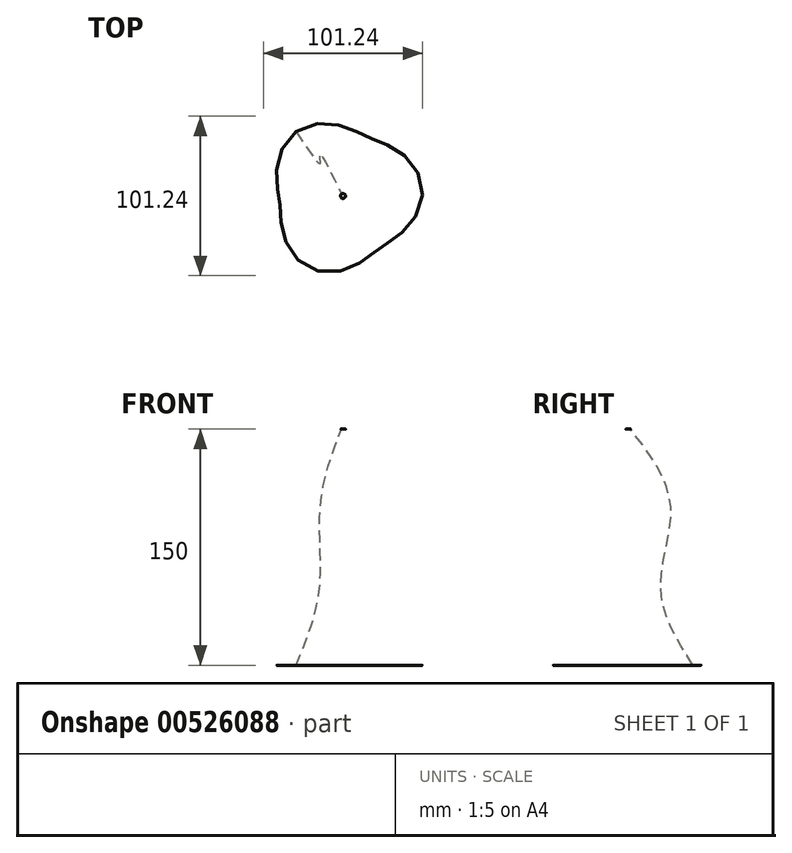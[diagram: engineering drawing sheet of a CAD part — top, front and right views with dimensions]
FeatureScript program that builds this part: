
annotation { "Feature Type Name" : "Feature", "Feature Type Description" : "" }
export const myFeature = defineFeature(function(context is Context, id is Id, definition is map)
    precondition{}
    {
        {
            var Q0;
            Q0=qCreatedBy(makeId("Top.planeOp"),FACE);
            var sketch = newSketch(context, id + "F0", { "sketchPlane" : qUnion([Q0])});
            skCircle(sketch, "E0.cCircle", {"center": v(0, 0) * mm, "radius": 50 * mm, "construction": true});
            skLineSegment(sketch, "E0.0", {"start": v(-40.96, 29.76) * mm, "end": v(-29.76, 40.96) * mm, "construction": true});
            skLineSegment(sketch, "E0.1", {"start": v(-29.76, 40.96) * mm, "end": v(-15.64, 48.15) * mm, "construction": true});
            skLineSegment(sketch, "E0.2", {"start": v(-15.64, 48.15) * mm, "end": v(0, 50.62) * mm, "construction": true});
            skLineSegment(sketch, "E0.3", {"start": v(0, 50.62) * mm, "end": v(15.64, 48.15) * mm, "construction": true});
            skLineSegment(sketch, "E0.4", {"start": v(15.64, 48.15) * mm, "end": v(29.76, 40.96) * mm, "construction": true});
            skLineSegment(sketch, "E0.5", {"start": v(29.76, 40.96) * mm, "end": v(40.96, 29.76) * mm, "construction": true});
            skLineSegment(sketch, "E0.6", {"start": v(40.96, 29.76) * mm, "end": v(48.15, 15.64) * mm, "construction": true});
            skLineSegment(sketch, "E0.7", {"start": v(48.15, 15.64) * mm, "end": v(50.62, 0) * mm, "construction": true});
            skLineSegment(sketch, "E0.8", {"start": v(50.62, 0) * mm, "end": v(48.15, -15.64) * mm, "construction": true});
            skLineSegment(sketch, "E0.9", {"start": v(48.15, -15.64) * mm, "end": v(40.96, -29.76) * mm, "construction": true});
            skLineSegment(sketch, "E0.10", {"start": v(40.96, -29.76) * mm, "end": v(29.76, -40.96) * mm, "construction": true});
            skLineSegment(sketch, "E0.11", {"start": v(29.76, -40.96) * mm, "end": v(15.64, -48.15) * mm, "construction": true});
            skLineSegment(sketch, "E0.12", {"start": v(15.64, -48.15) * mm, "end": v(0, -50.62) * mm, "construction": true});
            skLineSegment(sketch, "E0.13", {"start": v(0, -50.62) * mm, "end": v(-15.64, -48.15) * mm, "construction": true});
            skLineSegment(sketch, "E0.14", {"start": v(-15.64, -48.15) * mm, "end": v(-29.76, -40.96) * mm, "construction": true});
            skLineSegment(sketch, "E0.15", {"start": v(-29.76, -40.96) * mm, "end": v(-40.96, -29.76) * mm, "construction": true});
            skLineSegment(sketch, "E0.16", {"start": v(-40.96, -29.76) * mm, "end": v(-48.15, -15.64) * mm, "construction": true});
            skLineSegment(sketch, "E0.17", {"start": v(-48.15, -15.64) * mm, "end": v(-50.62, 0) * mm, "construction": true});
            skLineSegment(sketch, "E0.18", {"start": v(-50.62, 0) * mm, "end": v(-48.15, 15.64) * mm, "construction": true});
            skLineSegment(sketch, "E0.19", {"start": v(-48.15, 15.64) * mm, "end": v(-40.96, 29.76) * mm, "construction": true});
            skPoint(sketch, "E0.0.midPoint", {"position": v(-35.36, 35.36) * mm});
            skCircle(sketch, "E1.cCircle", {"center": v(0, 0) * mm, "radius": 40 * mm, "construction": true});
            skLineSegment(sketch, "E1.0", {"start": v(-18.39, 36.08) * mm, "end": v(-6.34, 40) * mm, "construction": true});
            skLineSegment(sketch, "E1.1", {"start": v(-6.34, 40) * mm, "end": v(6.34, 40) * mm, "construction": true});
            skLineSegment(sketch, "E1.2", {"start": v(6.34, 40) * mm, "end": v(18.39, 36.08) * mm, "construction": true});
            skLineSegment(sketch, "E1.3", {"start": v(18.39, 36.08) * mm, "end": v(28.64, 28.64) * mm, "construction": true});
            skLineSegment(sketch, "E1.4", {"start": v(28.64, 28.64) * mm, "end": v(36.08, 18.39) * mm, "construction": true});
            skLineSegment(sketch, "E1.5", {"start": v(36.08, 18.39) * mm, "end": v(40, 6.34) * mm, "construction": true});
            skLineSegment(sketch, "E1.6", {"start": v(40, 6.34) * mm, "end": v(40, -6.34) * mm, "construction": true});
            skLineSegment(sketch, "E1.7", {"start": v(40, -6.34) * mm, "end": v(36.08, -18.39) * mm, "construction": true});
            skLineSegment(sketch, "E1.8", {"start": v(36.08, -18.39) * mm, "end": v(28.64, -28.64) * mm, "construction": true});
            skLineSegment(sketch, "E1.9", {"start": v(28.64, -28.64) * mm, "end": v(18.39, -36.08) * mm, "construction": true});
            skLineSegment(sketch, "E1.10", {"start": v(18.39, -36.08) * mm, "end": v(6.34, -40) * mm, "construction": true});
            skLineSegment(sketch, "E1.11", {"start": v(6.34, -40) * mm, "end": v(-6.34, -40) * mm, "construction": true});
            skLineSegment(sketch, "E1.12", {"start": v(-6.34, -40) * mm, "end": v(-18.39, -36.08) * mm, "construction": true});
            skLineSegment(sketch, "E1.13", {"start": v(-18.39, -36.08) * mm, "end": v(-28.64, -28.64) * mm, "construction": true});
            skLineSegment(sketch, "E1.14", {"start": v(-28.64, -28.64) * mm, "end": v(-36.08, -18.39) * mm, "construction": true});
            skLineSegment(sketch, "E1.15", {"start": v(-36.08, -18.39) * mm, "end": v(-40, -6.34) * mm, "construction": true});
            skLineSegment(sketch, "E1.16", {"start": v(-40, -6.34) * mm, "end": v(-40, 6.34) * mm, "construction": true});
            skLineSegment(sketch, "E1.17", {"start": v(-40, 6.34) * mm, "end": v(-36.08, 18.39) * mm, "construction": true});
            skLineSegment(sketch, "E1.18", {"start": v(-36.08, 18.39) * mm, "end": v(-28.64, 28.64) * mm, "construction": true});
            skLineSegment(sketch, "E1.19", {"start": v(-28.64, 28.64) * mm, "end": v(-18.39, 36.08) * mm, "construction": true});
            skPoint(sketch, "E1.0.midPoint", {"position": v(-12.36, 38.04) * mm});
            skLineSegment(sketch, "E2", {"start": v(0, 0) * mm, "end": v(0, 40) * mm, "construction": true});
            skFitSpline(sketch, "E3", {"points": [v(-29.76, 40.96) * mm, v(-18.39, 36.08) * mm, v(-15.64, 48.15) * mm, v(-6.34, 40) * mm, v(0, 50.62) * mm, v(6.34, 40) * mm, v(15.64, 48.15) * mm, v(18.39, 36.08) * mm, v(29.76, 40.96) * mm, v(28.64, 28.64) * mm, v(40.96, 29.76) * mm, v(36.08, 18.39) * mm, v(48.15, 15.64) * mm, v(40, 6.34) * mm, v(50.62, 0) * mm, v(40, -6.34) * mm, v(48.15, -15.64) * mm, v(36.08, -18.39) * mm, v(40.96, -29.76) * mm, v(28.64, -28.64) * mm, v(29.76, -40.96) * mm, v(18.39, -36.08) * mm, v(15.64, -48.15) * mm, v(6.34, -40) * mm, v(0, -50.62) * mm, v(-6.34, -40) * mm, v(-15.64, -48.15) * mm, v(-18.39, -36.08) * mm, v(-29.76, -40.96) * mm, v(-28.64, -28.64) * mm, v(-40.96, -29.76) * mm, v(-36.08, -18.39) * mm, v(-48.15, -15.64) * mm, v(-40, -6.34) * mm, v(-50.62, 0) * mm, v(-40, 6.34) * mm, v(-48.15, 15.64) * mm, v(-36.08, 18.39) * mm, v(-40.96, 29.76) * mm, v(-28.64, 28.64) * mm, v(-29.76, 40.96) * mm]});
            skSolve(sketch);
        }
        {
            var Q0;
            Q0=qCreatedBy(makeId("Top.planeOp"),FACE);
            cPlane(context, id + "F1", {"entities" : qUnion([Q0]), "cplaneType" : CPlaneType.OFFSET, "offset" : 50 * mm, "width" : 150 * mm, "height" : 150 * mm});
        }
        {
            var Q0;
            Q0=qCreatedBy(id+"F1.planeOp",FACE);
            var sketch = newSketch(context, id + "F2", { "sketchPlane" : qUnion([Q0])});
            skCircle(sketch, "E4.cCircle", {"center": v(0, 0) * mm, "radius": 25 * mm, "construction": true});
            skLineSegment(sketch, "E4.0", {"start": v(-20.48, 14.88) * mm, "end": v(-14.88, 20.48) * mm, "construction": true});
            skLineSegment(sketch, "E4.1", {"start": v(-14.88, 20.48) * mm, "end": v(-7.82, 24.07) * mm, "construction": true});
            skLineSegment(sketch, "E4.2", {"start": v(-7.82, 24.07) * mm, "end": v(0, 25.31) * mm, "construction": true});
            skLineSegment(sketch, "E4.3", {"start": v(0, 25.31) * mm, "end": v(7.82, 24.07) * mm, "construction": true});
            skLineSegment(sketch, "E4.4", {"start": v(7.82, 24.07) * mm, "end": v(14.88, 20.48) * mm, "construction": true});
            skLineSegment(sketch, "E4.5", {"start": v(14.88, 20.48) * mm, "end": v(20.48, 14.88) * mm, "construction": true});
            skLineSegment(sketch, "E4.6", {"start": v(20.48, 14.88) * mm, "end": v(24.07, 7.82) * mm, "construction": true});
            skLineSegment(sketch, "E4.7", {"start": v(24.07, 7.82) * mm, "end": v(25.31, 0) * mm, "construction": true});
            skLineSegment(sketch, "E4.8", {"start": v(25.31, 0) * mm, "end": v(24.07, -7.82) * mm, "construction": true});
            skLineSegment(sketch, "E4.9", {"start": v(24.07, -7.82) * mm, "end": v(20.48, -14.88) * mm, "construction": true});
            skLineSegment(sketch, "E4.10", {"start": v(20.48, -14.88) * mm, "end": v(14.88, -20.48) * mm, "construction": true});
            skLineSegment(sketch, "E4.11", {"start": v(14.88, -20.48) * mm, "end": v(7.82, -24.07) * mm, "construction": true});
            skLineSegment(sketch, "E4.12", {"start": v(7.82, -24.07) * mm, "end": v(0, -25.31) * mm, "construction": true});
            skLineSegment(sketch, "E4.13", {"start": v(0, -25.31) * mm, "end": v(-7.82, -24.07) * mm, "construction": true});
            skLineSegment(sketch, "E4.14", {"start": v(-7.82, -24.07) * mm, "end": v(-14.88, -20.48) * mm, "construction": true});
            skLineSegment(sketch, "E4.15", {"start": v(-14.88, -20.48) * mm, "end": v(-20.48, -14.88) * mm, "construction": true});
            skLineSegment(sketch, "E4.16", {"start": v(-20.48, -14.88) * mm, "end": v(-24.07, -7.82) * mm, "construction": true});
            skLineSegment(sketch, "E4.17", {"start": v(-24.07, -7.82) * mm, "end": v(-25.31, 0) * mm, "construction": true});
            skLineSegment(sketch, "E4.18", {"start": v(-25.31, 0) * mm, "end": v(-24.07, 7.82) * mm, "construction": true});
            skLineSegment(sketch, "E4.19", {"start": v(-24.07, 7.82) * mm, "end": v(-20.48, 14.88) * mm, "construction": true});
            skPoint(sketch, "E4.0.midPoint", {"position": v(-17.68, 17.68) * mm});
            skCircle(sketch, "E5.cCircle", {"center": v(0, 0) * mm, "radius": 20 * mm, "construction": true});
            skLineSegment(sketch, "E5.0", {"start": v(-9.2, 18.04) * mm, "end": v(-3.17, 20) * mm, "construction": true});
            skLineSegment(sketch, "E5.1", {"start": v(-3.17, 20) * mm, "end": v(3.17, 20) * mm, "construction": true});
            skLineSegment(sketch, "E5.2", {"start": v(3.17, 20) * mm, "end": v(9.2, 18.04) * mm, "construction": true});
            skLineSegment(sketch, "E5.3", {"start": v(9.2, 18.04) * mm, "end": v(14.32, 14.32) * mm, "construction": true});
            skLineSegment(sketch, "E5.4", {"start": v(14.32, 14.32) * mm, "end": v(18.04, 9.2) * mm, "construction": true});
            skLineSegment(sketch, "E5.5", {"start": v(18.04, 9.2) * mm, "end": v(20, 3.17) * mm, "construction": true});
            skLineSegment(sketch, "E5.6", {"start": v(20, 3.17) * mm, "end": v(20, -3.17) * mm, "construction": true});
            skLineSegment(sketch, "E5.7", {"start": v(20, -3.17) * mm, "end": v(18.04, -9.2) * mm, "construction": true});
            skLineSegment(sketch, "E5.8", {"start": v(18.04, -9.2) * mm, "end": v(14.32, -14.32) * mm, "construction": true});
            skLineSegment(sketch, "E5.9", {"start": v(14.32, -14.32) * mm, "end": v(9.2, -18.04) * mm, "construction": true});
            skLineSegment(sketch, "E5.10", {"start": v(9.2, -18.04) * mm, "end": v(3.17, -20) * mm, "construction": true});
            skLineSegment(sketch, "E5.11", {"start": v(3.17, -20) * mm, "end": v(-3.17, -20) * mm, "construction": true});
            skLineSegment(sketch, "E5.12", {"start": v(-3.17, -20) * mm, "end": v(-9.2, -18.04) * mm, "construction": true});
            skLineSegment(sketch, "E5.13", {"start": v(-9.2, -18.04) * mm, "end": v(-14.32, -14.32) * mm, "construction": true});
            skLineSegment(sketch, "E5.14", {"start": v(-14.32, -14.32) * mm, "end": v(-18.04, -9.2) * mm, "construction": true});
            skLineSegment(sketch, "E5.15", {"start": v(-18.04, -9.2) * mm, "end": v(-20, -3.17) * mm, "construction": true});
            skLineSegment(sketch, "E5.16", {"start": v(-20, -3.17) * mm, "end": v(-20, 3.17) * mm, "construction": true});
            skLineSegment(sketch, "E5.17", {"start": v(-20, 3.17) * mm, "end": v(-18.04, 9.2) * mm, "construction": true});
            skLineSegment(sketch, "E5.18", {"start": v(-18.04, 9.2) * mm, "end": v(-14.32, 14.32) * mm, "construction": true});
            skLineSegment(sketch, "E5.19", {"start": v(-14.32, 14.32) * mm, "end": v(-9.2, 18.04) * mm, "construction": true});
            skPoint(sketch, "E5.0.midPoint", {"position": v(-6.18, 19.02) * mm});
            skLineSegment(sketch, "E6", {"start": v(0, 0) * mm, "end": v(0, 20) * mm, "construction": true});
            skFitSpline(sketch, "E7", {"points": [v(-14.88, 20.48) * mm, v(-9.2, 18.04) * mm, v(-7.82, 24.07) * mm, v(-3.17, 20) * mm, v(0, 25.31) * mm, v(3.17, 20) * mm, v(7.82, 24.07) * mm, v(9.2, 18.04) * mm, v(14.88, 20.48) * mm, v(14.32, 14.32) * mm, v(20.48, 14.88) * mm, v(18.04, 9.2) * mm, v(24.07, 7.82) * mm, v(20, 3.17) * mm, v(25.31, 0) * mm, v(20, -3.17) * mm, v(24.07, -7.82) * mm, v(18.04, -9.2) * mm, v(20.48, -14.88) * mm, v(14.32, -14.32) * mm, v(14.88, -20.48) * mm, v(9.2, -18.04) * mm, v(7.82, -24.07) * mm, v(3.17, -20) * mm, v(0, -25.31) * mm, v(-3.17, -20) * mm, v(-7.82, -24.07) * mm, v(-9.2, -18.04) * mm, v(-14.88, -20.48) * mm, v(-14.32, -14.32) * mm, v(-20.48, -14.88) * mm, v(-18.04, -9.2) * mm, v(-24.07, -7.82) * mm, v(-20, -3.17) * mm, v(-25.31, 0) * mm, v(-20, 3.17) * mm, v(-24.07, 7.82) * mm, v(-18.04, 9.2) * mm, v(-20.48, 14.88) * mm, v(-14.32, 14.32) * mm, v(-14.88, 20.48) * mm]});
            skSolve(sketch);
        }
        {
            var Q0;
            Q0=qCreatedBy(id+"F1.planeOp",FACE);
            cPlane(context, id + "F3", {"entities" : qUnion([Q0]), "cplaneType" : CPlaneType.OFFSET, "offset" : 50 * mm, "width" : 150 * mm, "height" : 150 * mm});
        }
        {
            var Q0;
            Q0=qCreatedBy(id+"F3.planeOp",FACE);
            var sketch = newSketch(context, id + "F4", { "sketchPlane" : qUnion([Q0])});
            skCircle(sketch, "E8.cCircle", {"center": v(0, 0) * mm, "radius": 40 * mm, "construction": true});
            skLineSegment(sketch, "E8.0", {"start": v(-32.76, 23.8) * mm, "end": v(-23.8, 32.76) * mm, "construction": true});
            skLineSegment(sketch, "E8.1", {"start": v(-23.8, 32.76) * mm, "end": v(-12.51, 38.52) * mm, "construction": true});
            skLineSegment(sketch, "E8.2", {"start": v(-12.51, 38.52) * mm, "end": v(0, 40.5) * mm, "construction": true});
            skLineSegment(sketch, "E8.3", {"start": v(0, 40.5) * mm, "end": v(12.51, 38.52) * mm, "construction": true});
            skLineSegment(sketch, "E8.4", {"start": v(12.51, 38.52) * mm, "end": v(23.8, 32.76) * mm, "construction": true});
            skLineSegment(sketch, "E8.5", {"start": v(23.8, 32.76) * mm, "end": v(32.76, 23.8) * mm, "construction": true});
            skLineSegment(sketch, "E8.6", {"start": v(32.76, 23.8) * mm, "end": v(38.52, 12.51) * mm, "construction": true});
            skLineSegment(sketch, "E8.7", {"start": v(38.52, 12.51) * mm, "end": v(40.5, 0) * mm, "construction": true});
            skLineSegment(sketch, "E8.8", {"start": v(40.5, 0) * mm, "end": v(38.52, -12.51) * mm, "construction": true});
            skLineSegment(sketch, "E8.9", {"start": v(38.52, -12.51) * mm, "end": v(32.76, -23.8) * mm, "construction": true});
            skLineSegment(sketch, "E8.10", {"start": v(32.76, -23.8) * mm, "end": v(23.8, -32.76) * mm, "construction": true});
            skLineSegment(sketch, "E8.11", {"start": v(23.8, -32.76) * mm, "end": v(12.51, -38.52) * mm, "construction": true});
            skLineSegment(sketch, "E8.12", {"start": v(12.51, -38.52) * mm, "end": v(0, -40.5) * mm, "construction": true});
            skLineSegment(sketch, "E8.13", {"start": v(0, -40.5) * mm, "end": v(-12.51, -38.52) * mm, "construction": true});
            skLineSegment(sketch, "E8.14", {"start": v(-12.51, -38.52) * mm, "end": v(-23.8, -32.76) * mm, "construction": true});
            skLineSegment(sketch, "E8.15", {"start": v(-23.8, -32.76) * mm, "end": v(-32.76, -23.8) * mm, "construction": true});
            skLineSegment(sketch, "E8.16", {"start": v(-32.76, -23.8) * mm, "end": v(-38.52, -12.51) * mm, "construction": true});
            skLineSegment(sketch, "E8.17", {"start": v(-38.52, -12.51) * mm, "end": v(-40.5, 0) * mm, "construction": true});
            skLineSegment(sketch, "E8.18", {"start": v(-40.5, 0) * mm, "end": v(-38.52, 12.51) * mm, "construction": true});
            skLineSegment(sketch, "E8.19", {"start": v(-38.52, 12.51) * mm, "end": v(-32.76, 23.8) * mm, "construction": true});
            skPoint(sketch, "E8.0.midPoint", {"position": v(-28.28, 28.28) * mm});
            skCircle(sketch, "E9.cCircle", {"center": v(0, 0) * mm, "radius": 30 * mm, "construction": true});
            skLineSegment(sketch, "E9.0", {"start": v(-13.79, 27.06) * mm, "end": v(-4.75, 30) * mm, "construction": true});
            skLineSegment(sketch, "E9.1", {"start": v(-4.75, 30) * mm, "end": v(4.75, 30) * mm, "construction": true});
            skLineSegment(sketch, "E9.2", {"start": v(4.75, 30) * mm, "end": v(13.79, 27.06) * mm, "construction": true});
            skLineSegment(sketch, "E9.3", {"start": v(13.79, 27.06) * mm, "end": v(21.48, 21.48) * mm, "construction": true});
            skLineSegment(sketch, "E9.4", {"start": v(21.48, 21.48) * mm, "end": v(27.06, 13.79) * mm, "construction": true});
            skLineSegment(sketch, "E9.5", {"start": v(27.06, 13.79) * mm, "end": v(30, 4.75) * mm, "construction": true});
            skLineSegment(sketch, "E9.6", {"start": v(30, 4.75) * mm, "end": v(30, -4.75) * mm, "construction": true});
            skLineSegment(sketch, "E9.7", {"start": v(30, -4.75) * mm, "end": v(27.06, -13.79) * mm, "construction": true});
            skLineSegment(sketch, "E9.8", {"start": v(27.06, -13.79) * mm, "end": v(21.48, -21.48) * mm, "construction": true});
            skLineSegment(sketch, "E9.9", {"start": v(21.48, -21.48) * mm, "end": v(13.79, -27.06) * mm, "construction": true});
            skLineSegment(sketch, "E9.10", {"start": v(13.79, -27.06) * mm, "end": v(4.75, -30) * mm, "construction": true});
            skLineSegment(sketch, "E9.11", {"start": v(4.75, -30) * mm, "end": v(-4.75, -30) * mm, "construction": true});
            skLineSegment(sketch, "E9.12", {"start": v(-4.75, -30) * mm, "end": v(-13.79, -27.06) * mm, "construction": true});
            skLineSegment(sketch, "E9.13", {"start": v(-13.79, -27.06) * mm, "end": v(-21.48, -21.48) * mm, "construction": true});
            skLineSegment(sketch, "E9.14", {"start": v(-21.48, -21.48) * mm, "end": v(-27.06, -13.79) * mm, "construction": true});
            skLineSegment(sketch, "E9.15", {"start": v(-27.06, -13.79) * mm, "end": v(-30, -4.75) * mm, "construction": true});
            skLineSegment(sketch, "E9.16", {"start": v(-30, -4.75) * mm, "end": v(-30, 4.75) * mm, "construction": true});
            skLineSegment(sketch, "E9.17", {"start": v(-30, 4.75) * mm, "end": v(-27.06, 13.79) * mm, "construction": true});
            skLineSegment(sketch, "E9.18", {"start": v(-27.06, 13.79) * mm, "end": v(-21.48, 21.48) * mm, "construction": true});
            skLineSegment(sketch, "E9.19", {"start": v(-21.48, 21.48) * mm, "end": v(-13.79, 27.06) * mm, "construction": true});
            skPoint(sketch, "E9.0.midPoint", {"position": v(-9.27, 28.53) * mm});
            skLineSegment(sketch, "E10", {"start": v(0, 0) * mm, "end": v(0, 30) * mm, "construction": true});
            skFitSpline(sketch, "E11", {"points": [v(-23.8, 32.76) * mm, v(-13.79, 27.06) * mm, v(-12.51, 38.52) * mm, v(-4.75, 30) * mm, v(0, 40.5) * mm, v(4.75, 30) * mm, v(12.51, 38.52) * mm, v(13.79, 27.06) * mm, v(23.8, 32.76) * mm, v(21.48, 21.48) * mm, v(32.76, 23.8) * mm, v(27.06, 13.79) * mm, v(38.52, 12.51) * mm, v(30, 4.75) * mm, v(40.5, 0) * mm, v(30, -4.75) * mm, v(38.52, -12.51) * mm, v(27.06, -13.79) * mm, v(32.76, -23.8) * mm, v(21.48, -21.48) * mm, v(23.8, -32.76) * mm, v(13.79, -27.06) * mm, v(12.51, -38.52) * mm, v(4.75, -30) * mm, v(0, -40.5) * mm, v(-4.75, -30) * mm, v(-12.51, -38.52) * mm, v(-13.79, -27.06) * mm, v(-23.8, -32.76) * mm, v(-21.48, -21.48) * mm, v(-32.76, -23.8) * mm, v(-27.06, -13.79) * mm, v(-38.52, -12.51) * mm, v(-30, -4.75) * mm, v(-40.5, 0) * mm, v(-30, 4.75) * mm, v(-38.52, 12.51) * mm, v(-27.06, 13.79) * mm, v(-32.76, 23.8) * mm, v(-21.48, 21.48) * mm, v(-23.8, 32.76) * mm]});
            skSolve(sketch);
        }
        {
            var Q0;
            Q0=qCreatedBy(id+"F3.planeOp",FACE);
            cPlane(context, id + "F5", {"entities" : qUnion([Q0]), "cplaneType" : CPlaneType.OFFSET, "offset" : 50 * mm, "width" : 150 * mm, "height" : 150 * mm});
        }
        {
            var Q0;
            Q0=qCreatedBy(id+"F5.planeOp",FACE);
            var sketch = newSketch(context, id + "F6", { "sketchPlane" : qUnion([Q0])});
            skCircle(sketch, "E12.cCircle", {"center": v(0, 0) * mm, "radius": 1.65 * mm, "construction": true});
            skLineSegment(sketch, "E12.0", {"start": v(-1.35, 0.98) * mm, "end": v(-0.98, 1.35) * mm, "construction": true});
            skLineSegment(sketch, "E12.1", {"start": v(-0.98, 1.35) * mm, "end": v(-0.52, 1.59) * mm, "construction": true});
            skLineSegment(sketch, "E12.2", {"start": v(-0.52, 1.59) * mm, "end": v(0, 1.67) * mm, "construction": true});
            skLineSegment(sketch, "E12.3", {"start": v(0, 1.67) * mm, "end": v(0.52, 1.59) * mm, "construction": true});
            skLineSegment(sketch, "E12.4", {"start": v(0.52, 1.59) * mm, "end": v(0.98, 1.35) * mm, "construction": true});
            skLineSegment(sketch, "E12.5", {"start": v(0.98, 1.35) * mm, "end": v(1.35, 0.98) * mm, "construction": true});
            skLineSegment(sketch, "E12.6", {"start": v(1.35, 0.98) * mm, "end": v(1.59, 0.52) * mm, "construction": true});
            skLineSegment(sketch, "E12.7", {"start": v(1.59, 0.52) * mm, "end": v(1.67, 0) * mm, "construction": true});
            skLineSegment(sketch, "E12.8", {"start": v(1.67, 0) * mm, "end": v(1.59, -0.52) * mm, "construction": true});
            skLineSegment(sketch, "E12.9", {"start": v(1.59, -0.52) * mm, "end": v(1.35, -0.98) * mm, "construction": true});
            skLineSegment(sketch, "E12.10", {"start": v(1.35, -0.98) * mm, "end": v(0.98, -1.35) * mm, "construction": true});
            skLineSegment(sketch, "E12.11", {"start": v(0.98, -1.35) * mm, "end": v(0.52, -1.59) * mm, "construction": true});
            skLineSegment(sketch, "E12.12", {"start": v(0.52, -1.59) * mm, "end": v(0, -1.67) * mm, "construction": true});
            skLineSegment(sketch, "E12.13", {"start": v(0, -1.67) * mm, "end": v(-0.52, -1.59) * mm, "construction": true});
            skLineSegment(sketch, "E12.14", {"start": v(-0.52, -1.59) * mm, "end": v(-0.98, -1.35) * mm, "construction": true});
            skLineSegment(sketch, "E12.15", {"start": v(-0.98, -1.35) * mm, "end": v(-1.35, -0.98) * mm, "construction": true});
            skLineSegment(sketch, "E12.16", {"start": v(-1.35, -0.98) * mm, "end": v(-1.59, -0.52) * mm, "construction": true});
            skLineSegment(sketch, "E12.17", {"start": v(-1.59, -0.52) * mm, "end": v(-1.67, 0) * mm, "construction": true});
            skLineSegment(sketch, "E12.18", {"start": v(-1.67, 0) * mm, "end": v(-1.59, 0.52) * mm, "construction": true});
            skLineSegment(sketch, "E12.19", {"start": v(-1.59, 0.52) * mm, "end": v(-1.35, 0.98) * mm, "construction": true});
            skPoint(sketch, "E12.0.midPoint", {"position": v(-1.17, 1.17) * mm});
            skCircle(sketch, "E13.cCircle", {"center": v(0, 0) * mm, "radius": 1.5 * mm, "construction": true});
            skLineSegment(sketch, "E13.0", {"start": v(-0.69, 1.35) * mm, "end": v(-0.24, 1.5) * mm, "construction": true});
            skLineSegment(sketch, "E13.1", {"start": v(-0.24, 1.5) * mm, "end": v(0.24, 1.5) * mm, "construction": true});
            skLineSegment(sketch, "E13.2", {"start": v(0.24, 1.5) * mm, "end": v(0.69, 1.35) * mm, "construction": true});
            skLineSegment(sketch, "E13.3", {"start": v(0.69, 1.35) * mm, "end": v(1.07, 1.07) * mm, "construction": true});
            skLineSegment(sketch, "E13.4", {"start": v(1.07, 1.07) * mm, "end": v(1.35, 0.69) * mm, "construction": true});
            skLineSegment(sketch, "E13.5", {"start": v(1.35, 0.69) * mm, "end": v(1.5, 0.24) * mm, "construction": true});
            skLineSegment(sketch, "E13.6", {"start": v(1.5, 0.24) * mm, "end": v(1.5, -0.24) * mm, "construction": true});
            skLineSegment(sketch, "E13.7", {"start": v(1.5, -0.24) * mm, "end": v(1.35, -0.69) * mm, "construction": true});
            skLineSegment(sketch, "E13.8", {"start": v(1.35, -0.69) * mm, "end": v(1.07, -1.07) * mm, "construction": true});
            skLineSegment(sketch, "E13.9", {"start": v(1.07, -1.07) * mm, "end": v(0.69, -1.35) * mm, "construction": true});
            skLineSegment(sketch, "E13.10", {"start": v(0.69, -1.35) * mm, "end": v(0.24, -1.5) * mm, "construction": true});
            skLineSegment(sketch, "E13.11", {"start": v(0.24, -1.5) * mm, "end": v(-0.24, -1.5) * mm, "construction": true});
            skLineSegment(sketch, "E13.12", {"start": v(-0.24, -1.5) * mm, "end": v(-0.69, -1.35) * mm, "construction": true});
            skLineSegment(sketch, "E13.13", {"start": v(-0.69, -1.35) * mm, "end": v(-1.07, -1.07) * mm, "construction": true});
            skLineSegment(sketch, "E13.14", {"start": v(-1.07, -1.07) * mm, "end": v(-1.35, -0.69) * mm, "construction": true});
            skLineSegment(sketch, "E13.15", {"start": v(-1.35, -0.69) * mm, "end": v(-1.5, -0.24) * mm, "construction": true});
            skLineSegment(sketch, "E13.16", {"start": v(-1.5, -0.24) * mm, "end": v(-1.5, 0.24) * mm, "construction": true});
            skLineSegment(sketch, "E13.17", {"start": v(-1.5, 0.24) * mm, "end": v(-1.35, 0.69) * mm, "construction": true});
            skLineSegment(sketch, "E13.18", {"start": v(-1.35, 0.69) * mm, "end": v(-1.07, 1.07) * mm, "construction": true});
            skLineSegment(sketch, "E13.19", {"start": v(-1.07, 1.07) * mm, "end": v(-0.69, 1.35) * mm, "construction": true});
            skPoint(sketch, "E13.0.midPoint", {"position": v(-0.46, 1.43) * mm});
            skLineSegment(sketch, "E14", {"start": v(0, 0) * mm, "end": v(0, 1.5) * mm, "construction": true});
            skFitSpline(sketch, "E15", {"points": [v(-0.98, 1.35) * mm, v(-0.69, 1.35) * mm, v(-0.52, 1.59) * mm, v(-0.24, 1.5) * mm, v(0, 1.67) * mm, v(0.24, 1.5) * mm, v(0.52, 1.59) * mm, v(0.69, 1.35) * mm, v(0.98, 1.35) * mm, v(1.07, 1.07) * mm, v(1.35, 0.98) * mm, v(1.35, 0.69) * mm, v(1.59, 0.52) * mm, v(1.5, 0.24) * mm, v(1.67, 0) * mm, v(1.5, -0.24) * mm, v(1.59, -0.52) * mm, v(1.35, -0.69) * mm, v(1.35, -0.98) * mm, v(1.07, -1.07) * mm, v(0.98, -1.35) * mm, v(0.69, -1.35) * mm, v(0.52, -1.59) * mm, v(0.24, -1.5) * mm, v(0, -1.67) * mm, v(-0.24, -1.5) * mm, v(-0.52, -1.59) * mm, v(-0.69, -1.35) * mm, v(-0.98, -1.35) * mm, v(-1.07, -1.07) * mm, v(-1.35, -0.98) * mm, v(-1.35, -0.69) * mm, v(-1.59, -0.52) * mm, v(-1.5, -0.24) * mm, v(-1.67, 0) * mm, v(-1.5, 0.24) * mm, v(-1.59, 0.52) * mm, v(-1.35, 0.69) * mm, v(-1.35, 0.98) * mm, v(-1.07, 1.07) * mm, v(-0.98, 1.35) * mm]});
            skSolve(sketch);
        }
        {
            var Q0;
            Q0 = qSketchRegion(id + "F0", true);
            var Q1;
            Q1 = qSketchRegion(id + "F2", true);
            var Q2;
            Q2 = qSketchRegion(id + "F4", true);
            var Q3;
            Q3 = qSketchRegion(id + "F6", true);
            loft(context, id + "F7", {"sheetProfilesArray" : [{ "sheetProfileEntities" : qUnion([Q0]) }, { "sheetProfileEntities" : qUnion([Q1]) }, { "sheetProfileEntities" : qUnion([Q2]) }, { "sheetProfileEntities" : qUnion([Q3]) }]});
        }
    });
